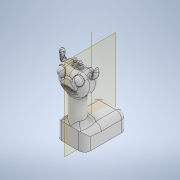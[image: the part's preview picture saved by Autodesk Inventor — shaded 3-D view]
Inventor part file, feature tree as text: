
AUTODESK INVENTOR PART (.ipt)
format: ipt  version: 2022 (Build 260153000, 153)  size: 1,917,440 bytes
history: native  units: mm
features: fillet x15, extrude x12, sketch x12, plane x5, mirror x1
ambient origin geometry x8: Origin, YZ Plane, XZ Plane, XY Plane, X Axis, Y Axis, Z Axis, Center Point
bodies: Solid1 (feature_tree), Solid2 (feature_tree)
feature tree (45):
  extrude  "Extrusion1"  Depth=30.0mm
  extrude  "Extrusion2"  Depth=15.0mm
  extrude  "Extrusion3"  Depth=2.0mm TaperAngle=0.0deg
  plane  "Work Plane2"
  extrude  "Extrusion4"  Depth=20.0mm
  fillet  "Fillet1"  Radius=20.0mm
  fillet  "Fillet2"  [1 undecoded]
  extrude  "Extrusion5"  Depth=12.0mm TaperAngle=0.0deg
  extrude  "Extrusion6"  Depth=4.0mm
  fillet  "Fillet4"  Radius=6.0mm
  plane  "Work Plane4"
  extrude  "Extrusion11"  Depth=6.0mm
  extrude  "Extrusion12"  Depth=2.0mm TaperAngle=0.0deg
  fillet  "Fillet5"  Radius=0.1mm
  extrude  "Extrusion13"  Depth=3.5mm TaperAngle=0.0deg
  fillet  "Fillet6"  Radius=2.5mm
  fillet  "Fillet7"  Radius=33.0mm
  plane  "Work Plane5"
  extrude  "Extrusion14"  Depth=3.0mm
  plane  "Work Plane6"
  extrude  "Extrusion15"  TaperAngle=0.0deg  [1 undecoded]
  fillet  "Fillet8"  [1 undecoded]
  fillet  "Fillet9"  Radius=2.1mm
  fillet  "Fillet10"  Radius=0.5mm
  fillet  "Fillet11"  Radius=2.1mm
  fillet  "Fillet12"  Radius=0.1mm
  fillet  "Fillet13"  Radius=2.0mm
  mirror  "Mirror1"
  fillet  "Fillet14"  Radius=3.0mm
  extrude  "Extrusion16"  Depth=1.0mm TaperAngle=0.0deg
  fillet  "Fillet15"  Radius=2.0mm
  fillet  "Fillet16"  Radius=1.0mm
  sketch  "Sketch1"  dims[d1=20.0mm d3=30.0mm]
  sketch  "Sketch2"  dims[d4=10.0mm d5=15.0mm]
  sketch  "Sketch3"  dims[d6=12.0mm d7=0.0mm d8=2.0mm d9=0.0mm]
  plane  "Work Plane1"
  sketch  "Sketch4"  dims[d10=10.0mm d11=10.0mm d12=20.0mm d13=0.0mm d14=-5.0mm]
  sketch  "Sketch5"  dims[d21=48.0mm d22=35.0mm d38=12.0mm d39=0.0mm]
  sketch  "Sketch6"  dims[d40=4.0mm d41=4.0mm d43=6.0mm]
  sketch  "Sketch12"  dims[d44=5.7mm d45=6.0mm]
  sketch  "Sketch13"  dims[d46=6.0mm d47=2.0mm d48=0.0mm d49=0.1mm]
  sketch  "Sketch14"  dims[d50=0.1mm d51=3.5mm d52=0.0mm d53=2.5mm d71=33.0mm]
  sketch  "Sketch15"  dims[d72=3.0mm d73=3.0mm]
  sketch  "Sketch17"  dims[d74=3.0mm d75=-2.268928mm d76=0.0mm d77=0.0mm d78=2.1mm d79=1.919862mm d80=0.5mm d81=2.1mm d82=-3.490659mm d83=0.1mm d84=2.0mm d85=3.0mm]
  sketch  "Sketch18"  dims[d86=3.0mm d87=-1.745329mm d88=3.0mm d89=0.0mm d90=2.0mm d91=1.0mm d92=1.0mm d93=0.58mm d94=0.58mm d95=0.58mm d96=0.5mm d97=2.0mm d98=0.0mm d99=2.0mm d100=1.0mm d63=0.0mm d64=0.0mm d65=0.0mm d66=0.0mm]
note: 3 required parameter values undecoded (feature->parameter linkage not recoverable at this tier; creation-order binding heuristic only, values carry confidence <= 0.55)
